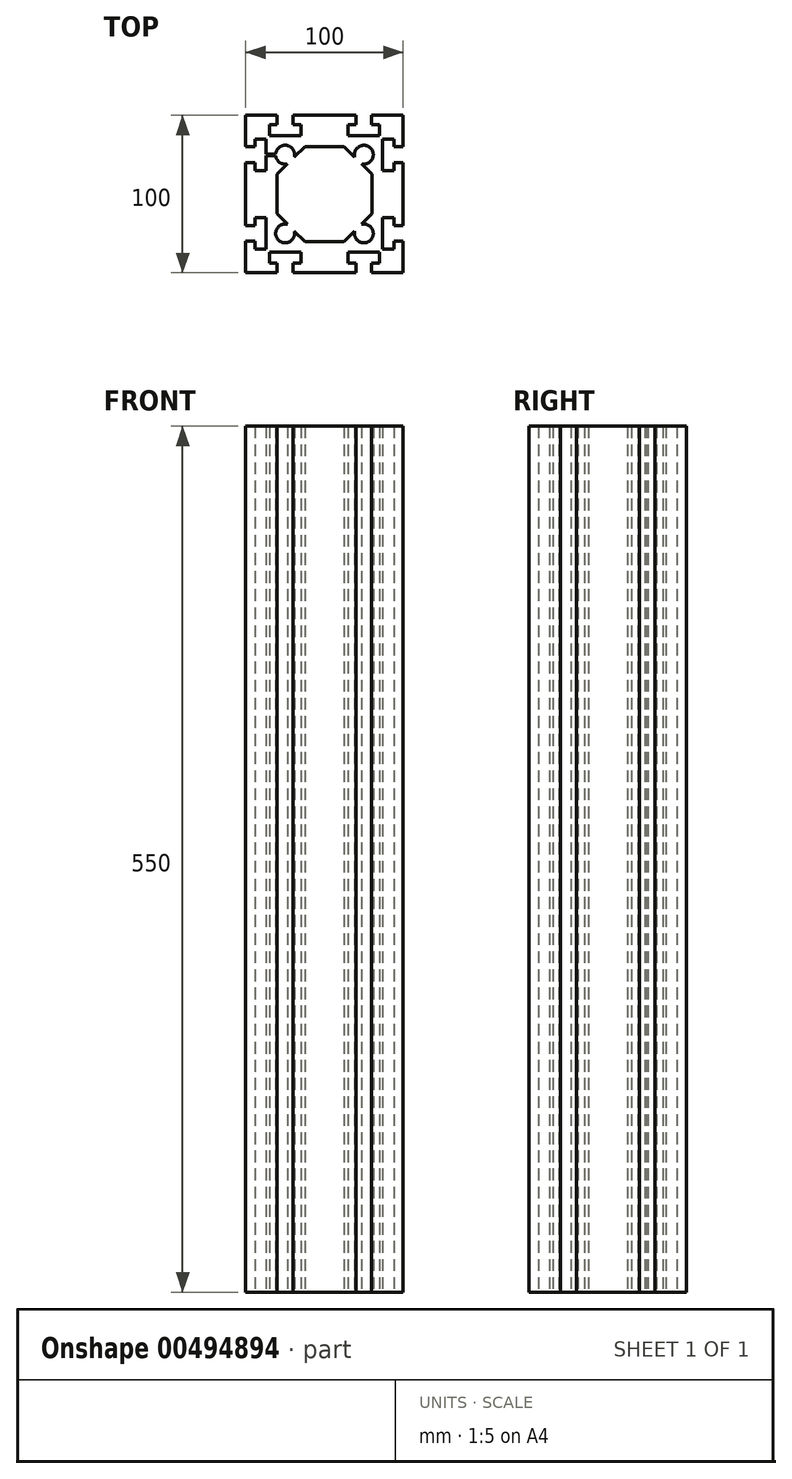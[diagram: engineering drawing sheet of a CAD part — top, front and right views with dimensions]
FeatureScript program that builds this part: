
annotation { "Feature Type Name" : "Feature", "Feature Type Description" : "" }
export const myFeature = defineFeature(function(context is Context, id is Id, definition is map)
    precondition{}
    {
        {
            var Q0;
            Q0=qCreatedBy(makeId("Top.planeOp"),FACE);
            var sketch = newSketch(context, id + "F0", { "sketchPlane" : qUnion([Q0])});
            skLineSegment(sketch, "E0.bottom", {"start": v(-50, 50) * mm, "end": v(-30, 50) * mm});
            skLineSegment(sketch, "E0.left", {"start": v(-50, 50) * mm, "end": v(-50, 30) * mm});
            skArc(sketch, "E1", {"start": v(-19.2, 23.48) * mm, "mid": v(-20.4, 28.86) * mm, "end": v(-25.5, 30.98) * mm});
            skArc(sketch, "E2", {"start": v(23.48, 19.2) * mm, "mid": v(29.24, 29.24) * mm, "end": v(19.2, 23.48) * mm});
            skArc(sketch, "E3", {"start": v(19.2, -23.48) * mm, "mid": v(29.24, -29.24) * mm, "end": v(23.48, -19.2) * mm});
            skArc(sketch, "E4", {"start": v(-23.48, -19.2) * mm, "mid": v(-29.24, -29.24) * mm, "end": v(-19.2, -23.48) * mm});
            skLineSegment(sketch, "E5.bottom", {"start": v(-44, 35) * mm, "end": v(-37, 35) * mm});
            skLineSegment(sketch, "E5.top", {"start": v(-44, 15) * mm, "end": v(-37, 15) * mm});
            skLineSegment(sketch, "E5.left", {"start": v(-44, 35) * mm, "end": v(-44, 30) * mm});
            skLineSegment(sketch, "E5.right", {"start": v(-37, 35) * mm, "end": v(-37, 25.5) * mm});
            skLineSegment(sketch, "E6", {"start": v(-44, 30) * mm, "end": v(-50, 30) * mm});
            skLineSegment(sketch, "E7", {"start": v(-44, 20) * mm, "end": v(-50, 20) * mm});
            skLineSegment(sketch, "E8.trimOffspring", {"start": v(-44, 20) * mm, "end": v(-44, 15) * mm});
            skLineSegment(sketch, "E9.1.0.0", {"start": v(-44, -35) * mm, "end": v(-37, -35) * mm});
            skLineSegment(sketch, "E9.1.0.1", {"start": v(-44, -15) * mm, "end": v(-37, -15) * mm});
            skLineSegment(sketch, "E9.1.0.2", {"start": v(-37, -15) * mm, "end": v(-37, -35) * mm});
            skLineSegment(sketch, "E9.1.0.3", {"start": v(-44, -15) * mm, "end": v(-44, -20) * mm});
            skLineSegment(sketch, "E9.1.0.4", {"start": v(-44, -20) * mm, "end": v(-50, -20) * mm});
            skLineSegment(sketch, "E9.1.0.5", {"start": v(-44, -30) * mm, "end": v(-44, -35) * mm});
            skLineSegment(sketch, "E9.1.0.6", {"start": v(-44, -30) * mm, "end": v(-50, -30) * mm});
            skLineSegment(sketch, "E10", {"start": v(-50, 20) * mm, "end": v(-50, -20) * mm});
            skLineSegment(sketch, "E11", {"start": v(-50, -30) * mm, "end": v(-50, -50) * mm});
            skLineSegment(sketch, "E12.bottom", {"start": v(-35, 44) * mm, "end": v(-30, 44) * mm});
            skLineSegment(sketch, "E12.top", {"start": v(-35, 37) * mm, "end": v(-25.5, 37) * mm});
            skLineSegment(sketch, "E12.left", {"start": v(-35, 44) * mm, "end": v(-35, 37) * mm});
            skLineSegment(sketch, "E12.right", {"start": v(-15, 44) * mm, "end": v(-15, 37) * mm});
            skLineSegment(sketch, "E13.left", {"start": v(-30, 50) * mm, "end": v(-30, 44) * mm});
            skLineSegment(sketch, "E13.right", {"start": v(-20, 50) * mm, "end": v(-20, 44) * mm});
            skLineSegment(sketch, "E14.trimOffspring", {"start": v(-20, 44) * mm, "end": v(-15, 44) * mm});
            skLineSegment(sketch, "E15.trimOffspring", {"start": v(-20, 50) * mm, "end": v(20, 50) * mm});
            skLineSegment(sketch, "E16.1.0.0", {"start": v(15, 44) * mm, "end": v(15, 37) * mm});
            skLineSegment(sketch, "E16.1.0.1", {"start": v(15, 44) * mm, "end": v(20, 44) * mm});
            skLineSegment(sketch, "E16.1.0.2", {"start": v(20, 50) * mm, "end": v(20, 44) * mm});
            skLineSegment(sketch, "E16.1.0.3", {"start": v(30, 44) * mm, "end": v(35, 44) * mm});
            skLineSegment(sketch, "E16.1.0.4", {"start": v(30, 50) * mm, "end": v(30, 44) * mm});
            skLineSegment(sketch, "E16.1.0.5", {"start": v(35, 44) * mm, "end": v(35, 37) * mm});
            skLineSegment(sketch, "E16.1.0.6", {"start": v(15, 37) * mm, "end": v(35, 37) * mm});
            skLineSegment(sketch, "E17.trimOffspring", {"start": v(30, 50) * mm, "end": v(50, 50) * mm});
            skLineSegment(sketch, "E18.MirrorCS", {"start": v(44, -30) * mm, "end": v(44, -35) * mm});
            skLineSegment(sketch, "E19.MirrorCS", {"start": v(44, -15) * mm, "end": v(44, -20) * mm});
            skLineSegment(sketch, "E20.MirrorCS", {"start": v(44, 30) * mm, "end": v(50, 30) * mm});
            skLineSegment(sketch, "E21.MirrorCS", {"start": v(44, 20) * mm, "end": v(50, 20) * mm});
            skLineSegment(sketch, "E22.MirrorCS", {"start": v(44, -30) * mm, "end": v(50, -30) * mm});
            skLineSegment(sketch, "E23.MirrorCS", {"start": v(44, -20) * mm, "end": v(50, -20) * mm});
            skLineSegment(sketch, "E24.MirrorCS", {"start": v(44, 35) * mm, "end": v(37, 35) * mm});
            skLineSegment(sketch, "E25.MirrorCS", {"start": v(44, 35) * mm, "end": v(44, 30) * mm});
            skLineSegment(sketch, "E26.MirrorCS", {"start": v(44, 20) * mm, "end": v(44, 15) * mm});
            skLineSegment(sketch, "E27.MirrorCS", {"start": v(37, 35) * mm, "end": v(37, 15) * mm});
            skLineSegment(sketch, "E28.MirrorCS", {"start": v(44, 15) * mm, "end": v(37, 15) * mm});
            skLineSegment(sketch, "E29.MirrorCS", {"start": v(37, -15) * mm, "end": v(37, -35) * mm});
            skLineSegment(sketch, "E30.MirrorCS", {"start": v(44, -15) * mm, "end": v(37, -15) * mm});
            skLineSegment(sketch, "E31.MirrorCS", {"start": v(44, -35) * mm, "end": v(37, -35) * mm});
            skLineSegment(sketch, "E32", {"start": v(50, 50) * mm, "end": v(50, 30) * mm});
            skLineSegment(sketch, "E33", {"start": v(50, 20) * mm, "end": v(50, -20) * mm});
            skLineSegment(sketch, "E34", {"start": v(50, -30) * mm, "end": v(50, -50) * mm});
            skLineSegment(sketch, "E35.MirrorCS", {"start": v(-35, -44) * mm, "end": v(-35, -37) * mm});
            skLineSegment(sketch, "E36.MirrorCS", {"start": v(-20, -50) * mm, "end": v(-20, -44) * mm});
            skLineSegment(sketch, "E37.MirrorCS", {"start": v(-30, -50) * mm, "end": v(-30, -44) * mm});
            skLineSegment(sketch, "E38.MirrorCS", {"start": v(30, -44) * mm, "end": v(35, -44) * mm});
            skLineSegment(sketch, "E39.MirrorCS", {"start": v(20, -50) * mm, "end": v(20, -44) * mm});
            skLineSegment(sketch, "E40.MirrorCS", {"start": v(35, -44) * mm, "end": v(35, -37) * mm});
            skLineSegment(sketch, "E41.MirrorCS", {"start": v(15, -44) * mm, "end": v(15, -37) * mm});
            skLineSegment(sketch, "E42.MirrorCS", {"start": v(15, -44) * mm, "end": v(20, -44) * mm});
            skLineSegment(sketch, "E43.MirrorCS", {"start": v(-20, -44) * mm, "end": v(-15, -44) * mm});
            skLineSegment(sketch, "E44.MirrorCS", {"start": v(30, -50) * mm, "end": v(30, -44) * mm});
            skLineSegment(sketch, "E45.MirrorCS", {"start": v(-15, -44) * mm, "end": v(-15, -37) * mm});
            skLineSegment(sketch, "E46.MirrorCS", {"start": v(-35, -44) * mm, "end": v(-30, -44) * mm});
            skLineSegment(sketch, "E47.MirrorCS", {"start": v(-50, -50) * mm, "end": v(-30, -50) * mm});
            skLineSegment(sketch, "E48.MirrorCS", {"start": v(30, -50) * mm, "end": v(50, -50) * mm});
            skLineSegment(sketch, "E49.MirrorCS", {"start": v(-35, -37) * mm, "end": v(-15, -37) * mm});
            skLineSegment(sketch, "E50.MirrorCS", {"start": v(-20, -50) * mm, "end": v(20, -50) * mm});
            skLineSegment(sketch, "E51.MirrorCS", {"start": v(15, -37) * mm, "end": v(35, -37) * mm});
            skLineSegment(sketch, "E52", {"start": v(12.5, 30.18) * mm, "end": v(19.2, 23.48) * mm});
            skLineSegment(sketch, "E53", {"start": v(30.18, 12.5) * mm, "end": v(30.18, -12.5) * mm});
            skLineSegment(sketch, "E54", {"start": v(30.18, -12.5) * mm, "end": v(23.48, -19.2) * mm});
            skLineSegment(sketch, "E55", {"start": v(12.5, -30.18) * mm, "end": v(-12.5, -30.18) * mm});
            skLineSegment(sketch, "E56", {"start": v(-12.5, -30.18) * mm, "end": v(-19.2, -23.48) * mm});
            skLineSegment(sketch, "E57", {"start": v(-30.18, -12.5) * mm, "end": v(-30.18, 12.5) * mm});
            skLineSegment(sketch, "E58", {"start": v(-30.18, 12.5) * mm, "end": v(-23.48, 19.2) * mm});
            skLineSegment(sketch, "E59", {"start": v(-12.5, 30.18) * mm, "end": v(12.5, 30.18) * mm});
            skLineSegment(sketch, "E60", {"start": v(0, 0) * mm, "end": v(-30.18, 0) * mm, "construction": true});
            skLineSegment(sketch, "E61", {"start": v(0, 0) * mm, "end": v(30.18, 0) * mm, "construction": true});
            skLineSegment(sketch, "E62", {"start": v(0, 0) * mm, "end": v(0, 30.18) * mm, "construction": true});
            skLineSegment(sketch, "E63", {"start": v(0, 0) * mm, "end": v(0, -30.18) * mm, "construction": true});
            skLineSegment(sketch, "E64.trimOffspring", {"start": v(-23.48, -19.2) * mm, "end": v(-30.18, -12.5) * mm});
            skLineSegment(sketch, "E65.trimOffspring", {"start": v(19.2, -23.48) * mm, "end": v(12.5, -30.18) * mm});
            skLineSegment(sketch, "E66.trimOffspring", {"start": v(23.48, 19.2) * mm, "end": v(30.18, 12.5) * mm});
            skLineSegment(sketch, "E67.trimOffspring", {"start": v(-19.2, 23.48) * mm, "end": v(-12.5, 30.18) * mm});
            skLineSegment(sketch, "E68", {"start": v(-37, 25.5) * mm, "end": v(-30.98, 25.5) * mm});
            skLineSegment(sketch, "E69", {"start": v(-30.98, 24.5) * mm, "end": v(-37, 24.5) * mm});
            skPoint(sketch, "E69.endSnap0", {"position": v(-37, 25) * mm});
            skArc(sketch, "E70.trimOffspring", {"start": v(-30.98, 24.5) * mm, "mid": v(-28.47, 20.1) * mm, "end": v(-23.48, 19.2) * mm});
            skLineSegment(sketch, "E71.trimOffspring", {"start": v(-37, 24.5) * mm, "end": v(-37, 15) * mm});
            skArc(sketch, "E72.trimOffspring", {"start": v(-25.5, 30.98) * mm, "mid": v(-29.24, 29.24) * mm, "end": v(-30.98, 25.5) * mm});
            skLineSegment(sketch, "E73.trimOffspring", {"start": v(-25.5, 37) * mm, "end": v(-15, 37) * mm});
            skSolve(sketch);
        }
        {
            var Q0;
            Q0=qSketchRegion(id+"F0",true);
            extrude(context, id + "F1", {"entities" : qUnion([Q0]), "depth" : 550 * mm});
        }
    });
